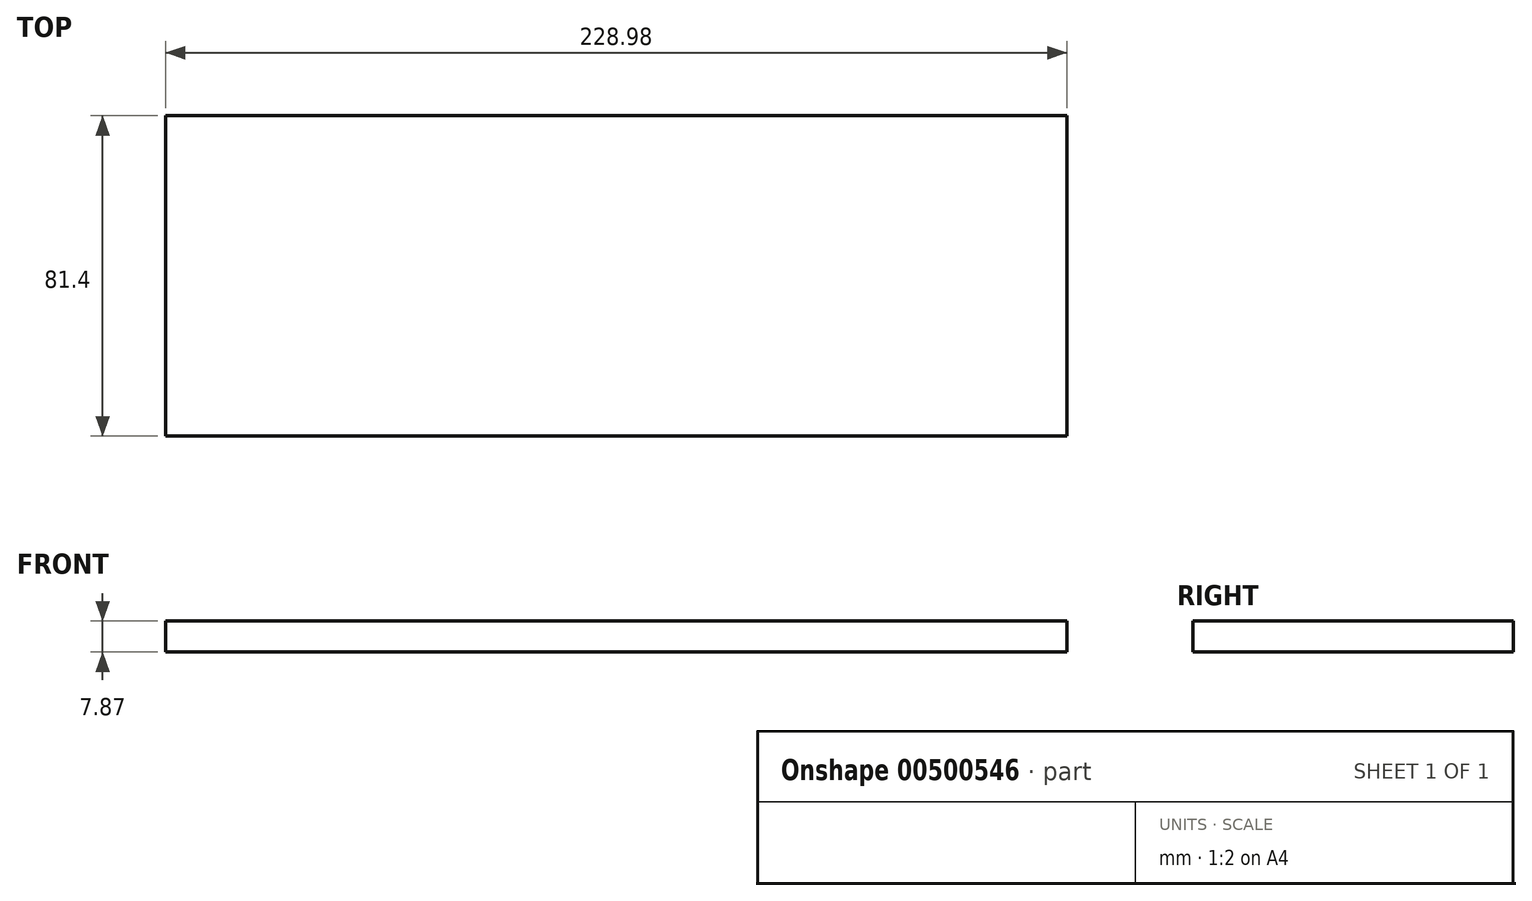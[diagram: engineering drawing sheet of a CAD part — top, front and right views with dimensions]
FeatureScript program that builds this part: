
annotation { "Feature Type Name" : "Feature", "Feature Type Description" : "" }
export const myFeature = defineFeature(function(context is Context, id is Id, definition is map)
    precondition{}
    {
        {
            var Q0;
            Q0=qCreatedBy(makeId("Top.planeOp"),FACE);
            var sketch = newSketch(context, id + "F0", { "sketchPlane" : qUnion([Q0])});
            skLineSegment(sketch, "E0.bottom", {"start": v(-108.6, 25.3) * mm, "end": v(120.39, 25.3) * mm});
            skLineSegment(sketch, "E0.top", {"start": v(-108.6, -56.1) * mm, "end": v(120.39, -56.1) * mm});
            skLineSegment(sketch, "E0.left", {"start": v(-108.6, 25.3) * mm, "end": v(-108.6, -56.1) * mm});
            skLineSegment(sketch, "E0.right", {"start": v(120.39, 25.3) * mm, "end": v(120.39, -56.1) * mm});
            skSolve(sketch);
        }
        {
            var Q0;
            Q0=makeQuery(id+"F0.imprint","IMPRINT",FACE,{"disambiguationData":[TD([[makeQuery(id+"F0.imprint","IMPRINT",EDGE,{"derivedFrom":sQuery(id+"F0.wireOp",EDGE,"E0.bottom")}),-1.0]])]});
            extrude(context, id + "F1", {"entities" : qUnion([Q0]), "depth" : 7.87 * mm});
        }
    });
